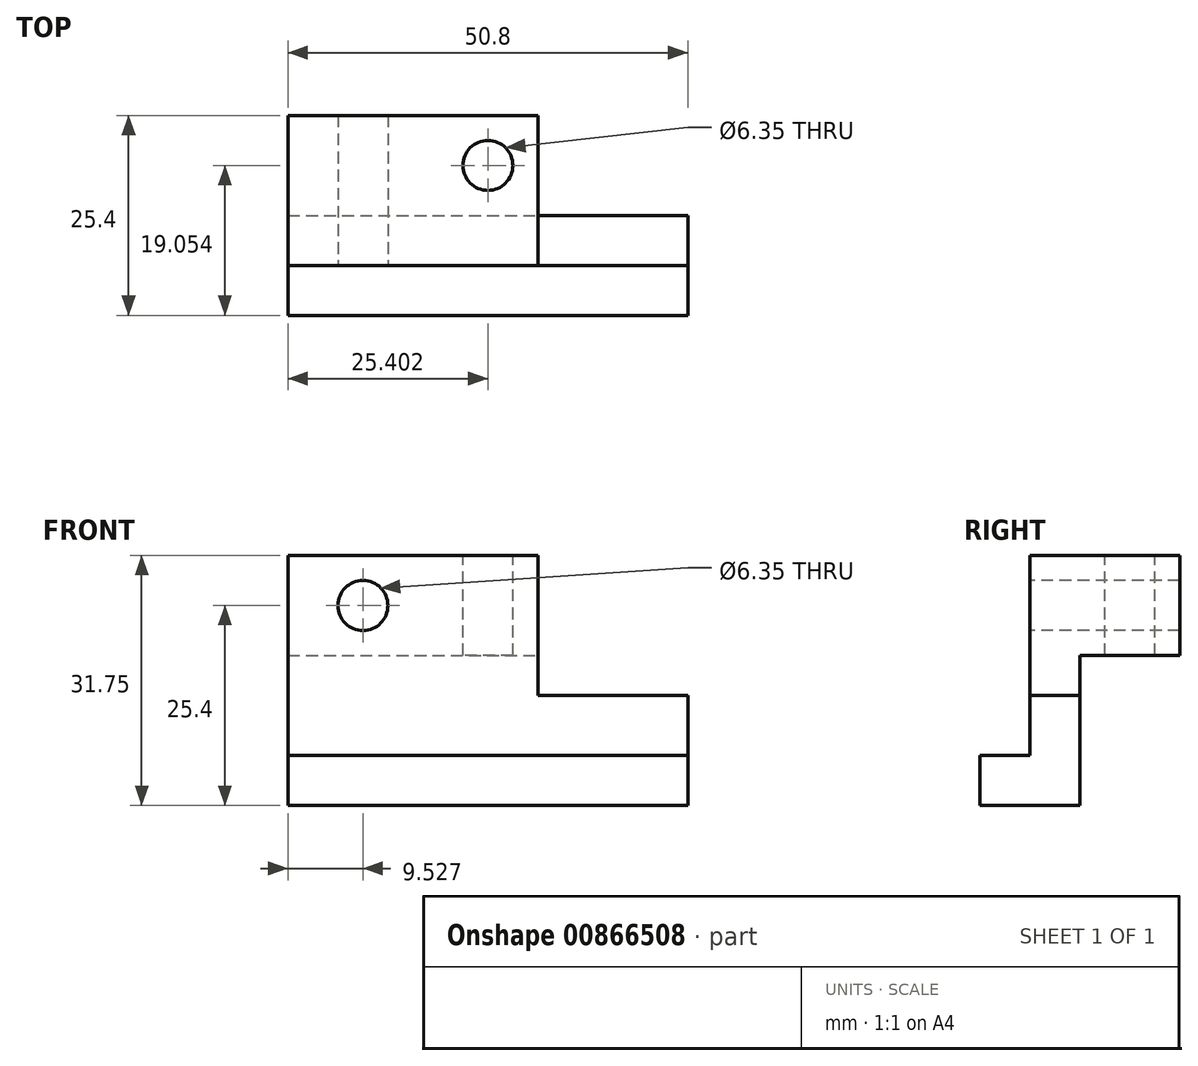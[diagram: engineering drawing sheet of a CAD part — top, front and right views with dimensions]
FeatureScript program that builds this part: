
annotation { "Feature Type Name" : "Feature", "Feature Type Description" : "" }
export const myFeature = defineFeature(function(context is Context, id is Id, definition is map)
    precondition{}
    {
        {
            var Q0;
            Q0=qCreatedBy(makeId("Top.planeOp"),FACE);
            var sketch = newSketch(context, id + "F0", { "sketchPlane" : qUnion([Q0])});
            skLineSegment(sketch, "E0.bottom", {"start": v(56.63, -10.37) * mm, "end": v(88.38, -10.37) * mm});
            skLineSegment(sketch, "E0.top", {"start": v(56.63, -29.42) * mm, "end": v(88.38, -29.42) * mm});
            skLineSegment(sketch, "E0.left", {"start": v(56.63, -10.37) * mm, "end": v(56.63, -29.42) * mm});
            skLineSegment(sketch, "E0.right", {"start": v(88.38, -10.37) * mm, "end": v(88.38, -29.42) * mm});
            skSolve(sketch);
        }
        {
            var Q0;
            Q0 = qSketchRegion(id + "F0", true);
            extrude(context, id + "F1", {"entities" : qUnion([Q0]), "depth" : 12.7 * mm, "offsetDistance" : 25.4 * mm});
        }
        {
            var Q0;
            Q0=makeQuery(id+"F1.opExtrude","SWEPT_FACE",FACE,{"disambiguationData":[OSD([sQuery(id+"F0.wireOp",EDGE,"E0.top")])]});
            var sketch = newSketch(context, id + "F2", { "sketchPlane" : qUnion([Q0])});
            skLineSegment(sketch, "E1.bottom", {"start": v(56.63, 0) * mm, "end": v(107.43, 0) * mm});
            skLineSegment(sketch, "E1.top", {"start": v(56.63, -12.7) * mm, "end": v(107.43, -12.7) * mm});
            skLineSegment(sketch, "E1.left", {"start": v(56.63, 0) * mm, "end": v(56.63, -12.7) * mm});
            skLineSegment(sketch, "E1.right", {"start": v(107.43, 0) * mm, "end": v(107.43, -12.7) * mm});
            skSolve(sketch);
        }
        {
            var Q0;
            Q0 = qSketchRegion(id + "F2", true);
            extrude(context, id + "F3", {"entities" : qUnion([Q0]), "operationType" : NewBodyOperationType.ADD, "oppositeDirection" : true, "depth" : 6.35 * mm, "offsetDistance" : 25.4 * mm});
        }
        {
            var Q0;
            Q0=makeQuery(id+"F3.boolean.opBoolean","MERGE",FACE,{"derivedFrom":[makeQuery(id+"F1.opExtrude","SWEPT_FACE",FACE,{"disambiguationData":[OSD([sQuery(id+"F0.wireOp",EDGE,"E0.top")])]}),makeQuery(id+"F3.opExtrude","CAP_FACE",FACE,{"disambiguationData":[OSD([sQuery(id+"F2.wireOp",EDGE,"E1.bottom"),sQuery(id+"F2.wireOp",EDGE,"E1.top"),sQuery(id+"F2.wireOp",EDGE,"E1.left"),sQuery(id+"F2.wireOp",EDGE,"E1.right")])],"isStart":true})]});
            var sketch = newSketch(context, id + "F4", { "sketchPlane" : qUnion([Q0])});
            skLineSegment(sketch, "E2.bottom", {"start": v(88.38, 0) * mm, "end": v(107.43, 0) * mm});
            skLineSegment(sketch, "E2.top", {"start": v(88.38, -5.09) * mm, "end": v(107.43, -5.09) * mm});
            skLineSegment(sketch, "E2.left", {"start": v(88.38, 0) * mm, "end": v(88.38, -5.09) * mm});
            skLineSegment(sketch, "E2.right", {"start": v(107.43, 0) * mm, "end": v(107.43, -5.09) * mm});
            skSolve(sketch);
        }
        {
            var Q0;
            Q0 = qSketchRegion(id + "F4", true);
            extrude(context, id + "F5", {"entities" : qUnion([Q0]), "operationType" : NewBodyOperationType.REMOVE, "oppositeDirection" : true, "depth" : 6.35 * mm, "offsetDistance" : 25.4 * mm});
        }
        {
            var Q0;
            Q0=makeQuery(id+"F3.opExtrude","SWEPT_FACE",FACE,{"disambiguationData":[OSD([sQuery(id+"F2.wireOp",EDGE,"E1.right")])]});
            var sketch = newSketch(context, id + "F6", { "sketchPlane" : qUnion([Q0])});
            skLineSegment(sketch, "E3.bottom", {"start": v(-23.07, -12.7) * mm, "end": v(-35.77, -12.7) * mm});
            skLineSegment(sketch, "E3.top", {"start": v(-23.07, -19.05) * mm, "end": v(-35.77, -19.05) * mm});
            skLineSegment(sketch, "E3.left", {"start": v(-23.07, -12.7) * mm, "end": v(-23.07, -19.05) * mm});
            skLineSegment(sketch, "E3.right", {"start": v(-35.77, -12.7) * mm, "end": v(-35.77, -19.05) * mm});
            skSolve(sketch);
        }
        {
            var Q0;
            Q0 = qSketchRegion(id + "F6", true);
            extrude(context, id + "F7", {"entities" : qUnion([Q0]), "operationType" : NewBodyOperationType.ADD, "oppositeDirection" : true, "depth" : 50.8 * mm, "offsetDistance" : 25.4 * mm});
        }
        {
            var Q0;
            {var subQ1=sQuery(id+"F0.wireOp",EDGE,"E0.top");Q0=makeQuery(id+"F2.imprint","IMPRINT",FACE,{"disambiguationData":[TD([[makeQuery(id+"F2.imprint","IMPRINT",EDGE,{"derivedFrom":makeQuery(id+"F1.opExtrude","CAP_EDGE",EDGE,{"disambiguationData":[OSD([subQ1])],"isStart":false})}),-1.0]])]});}
            var sketch = newSketch(context, id + "F8", { "sketchPlane" : qUnion([Q0])});
            skCircle(sketch, "E4", {"center": v(66.16, 6.35) * mm, "radius": 3.18 * mm});
            skSolve(sketch);
        }
        {
            var Q0;
            Q0=makeQuery(id+"F1.opExtrude","CAP_FACE",FACE,{"disambiguationData":[OSD([sQuery(id+"F0.wireOp",EDGE,"E0.bottom"),sQuery(id+"F0.wireOp",EDGE,"E0.top"),sQuery(id+"F0.wireOp",EDGE,"E0.left"),sQuery(id+"F0.wireOp",EDGE,"E0.right")])],"isStart":false});
            var sketch = newSketch(context, id + "F9", { "sketchPlane" : qUnion([Q0])});
            skCircle(sketch, "E5", {"center": v(82.03, -16.72) * mm, "radius": 3.18 * mm});
            skSolve(sketch);
        }
        {
            var Q0;
            Q0=makeQuery(id+"F9.imprint","IMPRINT",FACE,{"disambiguationData":[TD([[makeQuery(id+"F9.imprint","IMPRINT",EDGE,{"derivedFrom":sQuery(id+"F9.wireOp",EDGE,"E5")}),1.0]])]});
            extrude(context, id + "F10", {"entities" : qUnion([Q0]), "operationType" : NewBodyOperationType.REMOVE, "oppositeDirection" : true, "depth" : 12.7 * mm, "offsetDistance" : 25.4 * mm});
        }
        {
            var Q0;
            Q0=makeQuery(id+"F8.imprint","IMPRINT",FACE,{"disambiguationData":[TD([[makeQuery(id+"F8.imprint","IMPRINT",EDGE,{"derivedFrom":sQuery(id+"F8.wireOp",EDGE,"E4")}),1.0]])]});
            var Q1;
            Q1=sQuery(id+"F8.wireOp",EDGE,"E4");
            extrude(context, id + "F11", {"entities" : qUnion([Q0]), "operationType" : NewBodyOperationType.REMOVE, "surfaceEntities" : qUnion([Q1]), "oppositeDirection" : true, "depth" : 19.05 * mm, "offsetDistance" : 25.4 * mm});
        }
    });
